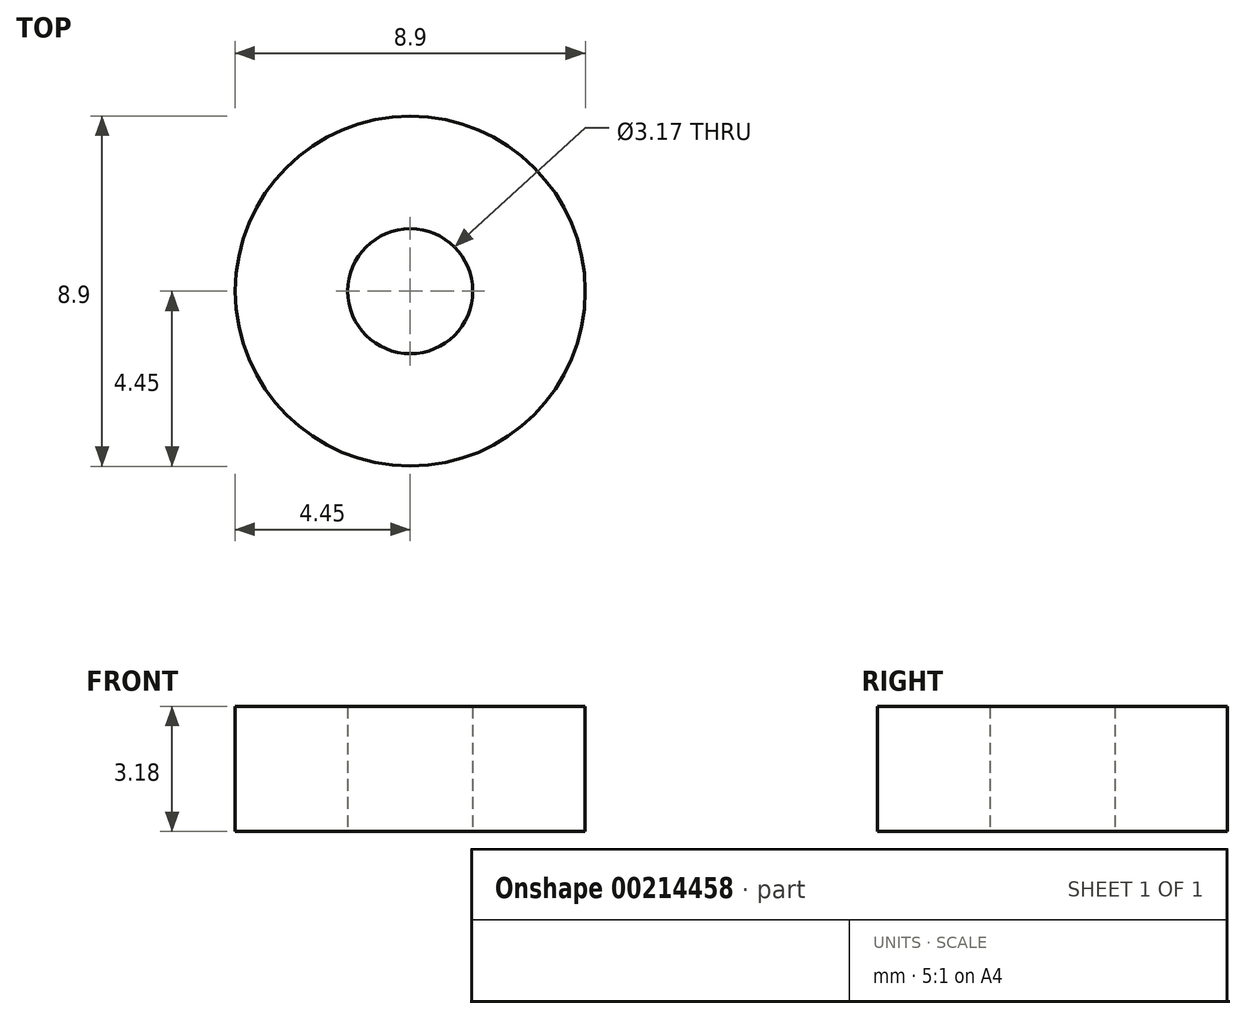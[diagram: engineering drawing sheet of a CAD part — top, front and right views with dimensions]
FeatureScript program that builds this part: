
annotation { "Feature Type Name" : "Feature", "Feature Type Description" : "" }
export const myFeature = defineFeature(function(context is Context, id is Id, definition is map)
    precondition{}
    {
        {
            var Q0;
            Q0=qCreatedBy(makeId("Top.planeOp"),FACE);
            var sketch = newSketch(context, id + "F0", { "sketchPlane" : qUnion([Q0])});
            skCircle(sketch, "E0", {"center": v(0, 0) * mm, "radius": 4.45 * mm});
            skCircle(sketch, "E1", {"center": v(0, 0) * mm, "radius": 1.59 * mm});
            skSolve(sketch);
        }
        {
            var Q0;
            Q0 = qSketchRegion(id + "F0", true);
            extrude(context, id + "F1", {"entities" : qUnion([Q0]), "depth" : 3.17 * mm});
        }
    });
